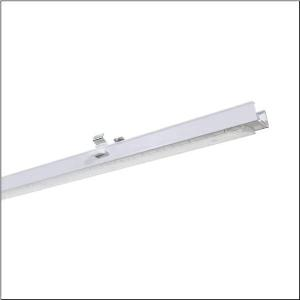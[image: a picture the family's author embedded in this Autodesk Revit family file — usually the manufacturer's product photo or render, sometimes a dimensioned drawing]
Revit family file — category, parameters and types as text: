
# Revit family: trunking_flex_31_51re12mb18b
name_source: partatom
category: Lighting Fixtures
units: mm (PartAtom-declared; Revit-internal decimal feet)

## family parameters
Cut with Voids When Loaded = No
Host = Face
Light Source = No
Part Type = Normal
Room Calculation Point = No
Round Connector Dimension = Use Diameter
Shared = No

## types (1)
- --- (1 x LED, 8000 lm, 50 W, 3500K)
    Apparent Load = 50 VA
    CIE Flux Codes = 65 91 98 99 100
    Color Rendering = 80
    Color Temperature = 3500K
    Default Elevation = 1800 mm
    Description = Trunking Flex 31, luminaire insert, of extruded aluminium section, coated, traffic white (RAL 9016), length: 1.472mm, width: 91mm, height: 53mm, LED rated luminous flux: 8.000lm, light colour: 835, control gear: ON/OFF Multilumen, with system connector: socket, mains connection: 220..240V, AC, 50/60Hz, rated input power: 50W, luminous flux adjustable on luminaire in four steps (4130/5610/6850/8000lm), connected load according to luminous flux setting (25/34/42/50W), primary light control with lens, of plastic, primary optical cover: cover, of PMMA, light emission: direct distribution, protection rating (complete): IP20, insulation class (complete): insulation class I (protective earthing), certification: CE, UKCA, impact resistance: IK02, permissible ambient temperature for indoor applications: -20..+40°C, packaging unit: 1 piece
    Height = 58 mm
    Lamp = 1 x LED
    Lamp Light Flux = 8000 lm
    Lamp Power = 50 W
    Lamp count = 1
    Length = 1472 mm
    Luminous efficacy = 160 lm/W
    Manufacturer = Siteco
    ModVariant = No
    Model = 51RE12MB18B
    Mounting Place = Ceiling
    Mounting Type = Pendant
    Number of Poles = 1
    OnlyDefault = Yes
    Power Factor = 1
    Product Name = Trunking Flex 31
    Product group = luminaire insert
    ProductGroupID = 901
    Protection Class = Protection class I
    Protection Degree = IP 20
    RLX_Detail_Level = 1
    RLX_Emergency_Light_Flux = 0 lm
    RLX_Emergency_Type = 0
    RLX_Emergency_Type_DB = No
    RlxData = <blob elided: 20325 chars, md5=932859ac>
    Socket = socket
    Standby Power = 0 W
    System Light Flux = 8000 lm
    System Power = 50 W
    Type Comments = factory setting: luminous flux: 100 % | (ON | ON) | 300 mA
    Type Image = l_1266702.jpg
    URL = http://relux.com
    VarID = @adj_001281
    Voltage = 0 V
    Weight = 0.00 kg
    Width = 65 mm

## geometry (parser evidence)
native form markers: Blend x4, Sweep x10
no freeform markers — native parametric forms only
